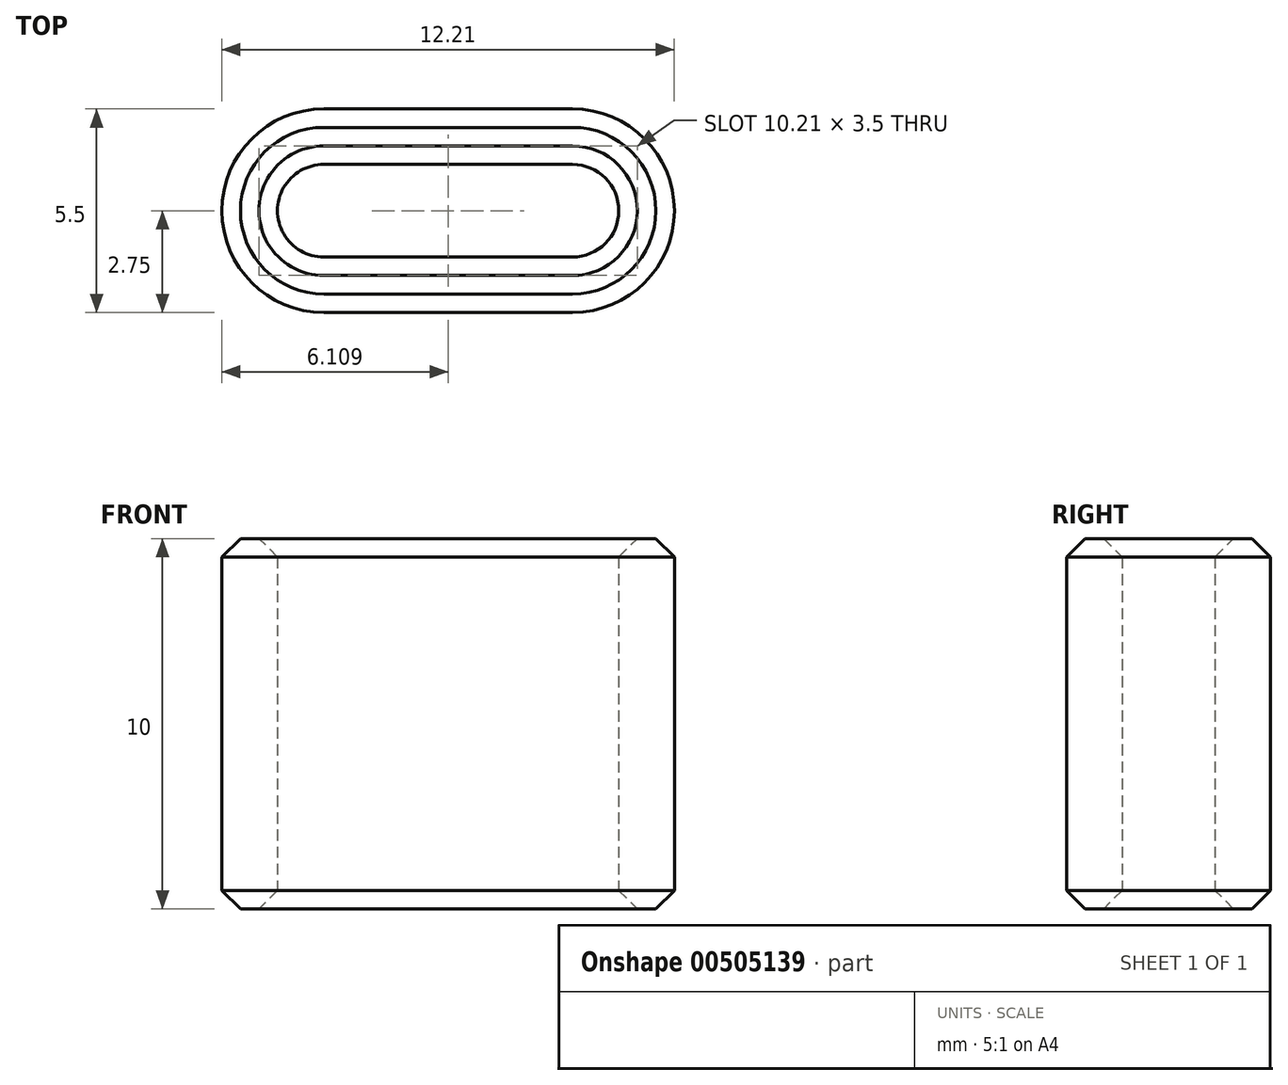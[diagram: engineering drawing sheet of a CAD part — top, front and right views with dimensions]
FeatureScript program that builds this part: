
annotation { "Feature Type Name" : "Feature", "Feature Type Description" : "" }
export const myFeature = defineFeature(function(context is Context, id is Id, definition is map)
    precondition{}
    {
        {
            var Q0;
            Q0=qCreatedBy(makeId("Top.planeOp"),FACE);
            var sketch = newSketch(context, id + "F0", { "sketchPlane" : qUnion([Q0])});
            skLineSegment(sketch, "E0.bottom", {"start": v(3.35, 1.25) * mm, "end": v(-3.36, 1.25) * mm});
            skLineSegment(sketch, "E0.top", {"start": v(3.36, -1.25) * mm, "end": v(-3.35, -1.25) * mm});
            skPoint(sketch, "E0.middle", {"position": v(0, 0) * mm});
            skArc(sketch, "E1", {"start": v(3.35, 1.25) * mm, "mid": v(4.6, 0) * mm, "end": v(3.36, -1.25) * mm});
            skArc(sketch, "E2", {"start": v(-3.36, 1.25) * mm, "mid": v(-4.6, 0) * mm, "end": v(-3.35, -1.25) * mm});
            skArc(sketch, "E3.0", {"start": v(-3.36, 2.75) * mm, "mid": v(-6.1, 0) * mm, "end": v(-3.36, -2.75) * mm});
            skLineSegment(sketch, "E3.1", {"start": v(3.35, 2.75) * mm, "end": v(-3.36, 2.75) * mm});
            skArc(sketch, "E3.2", {"start": v(3.35, 2.75) * mm, "mid": v(6.1, 0) * mm, "end": v(3.35, -2.75) * mm});
            skLineSegment(sketch, "E3.3", {"start": v(3.35, -2.75) * mm, "end": v(-3.36, -2.75) * mm});
            skSolve(sketch);
        }
        {
            var Q0;
            Q0 = qSketchRegion(id + "F0", true);
            extrude(context, id + "F1", {"entities" : qUnion([Q0]), "depth" : 10 * mm});
        }
        {
            var Q0;
            Q0=makeQuery(id+"F1.opExtrude","CAP_FACE",FACE,{"disambiguationData":[OSD([sQuery(id+"F0.wireOp",EDGE,"E0.bottom"),sQuery(id+"F0.wireOp",EDGE,"E0.top"),sQuery(id+"F0.wireOp",EDGE,"E1"),sQuery(id+"F0.wireOp",EDGE,"E2"),sQuery(id+"F0.wireOp",EDGE,"E3.0"),sQuery(id+"F0.wireOp",EDGE,"E3.1"),sQuery(id+"F0.wireOp",EDGE,"E3.2"),sQuery(id+"F0.wireOp",EDGE,"E3.3")])],"isStart":false});
            var Q1;
            Q1=makeQuery(id+"F1.opExtrude","CAP_FACE",FACE,{"disambiguationData":[OSD([sQuery(id+"F0.wireOp",EDGE,"E0.bottom"),sQuery(id+"F0.wireOp",EDGE,"E0.top"),sQuery(id+"F0.wireOp",EDGE,"E1"),sQuery(id+"F0.wireOp",EDGE,"E2"),sQuery(id+"F0.wireOp",EDGE,"E3.0"),sQuery(id+"F0.wireOp",EDGE,"E3.1"),sQuery(id+"F0.wireOp",EDGE,"E3.2"),sQuery(id+"F0.wireOp",EDGE,"E3.3")])],"isStart":true});
            chamfer(context, id + "F2", {"entities" : qUnion([Q0, Q1]), "width" : .5 * mm, "tangentPropagation" : true});
        }
    });
